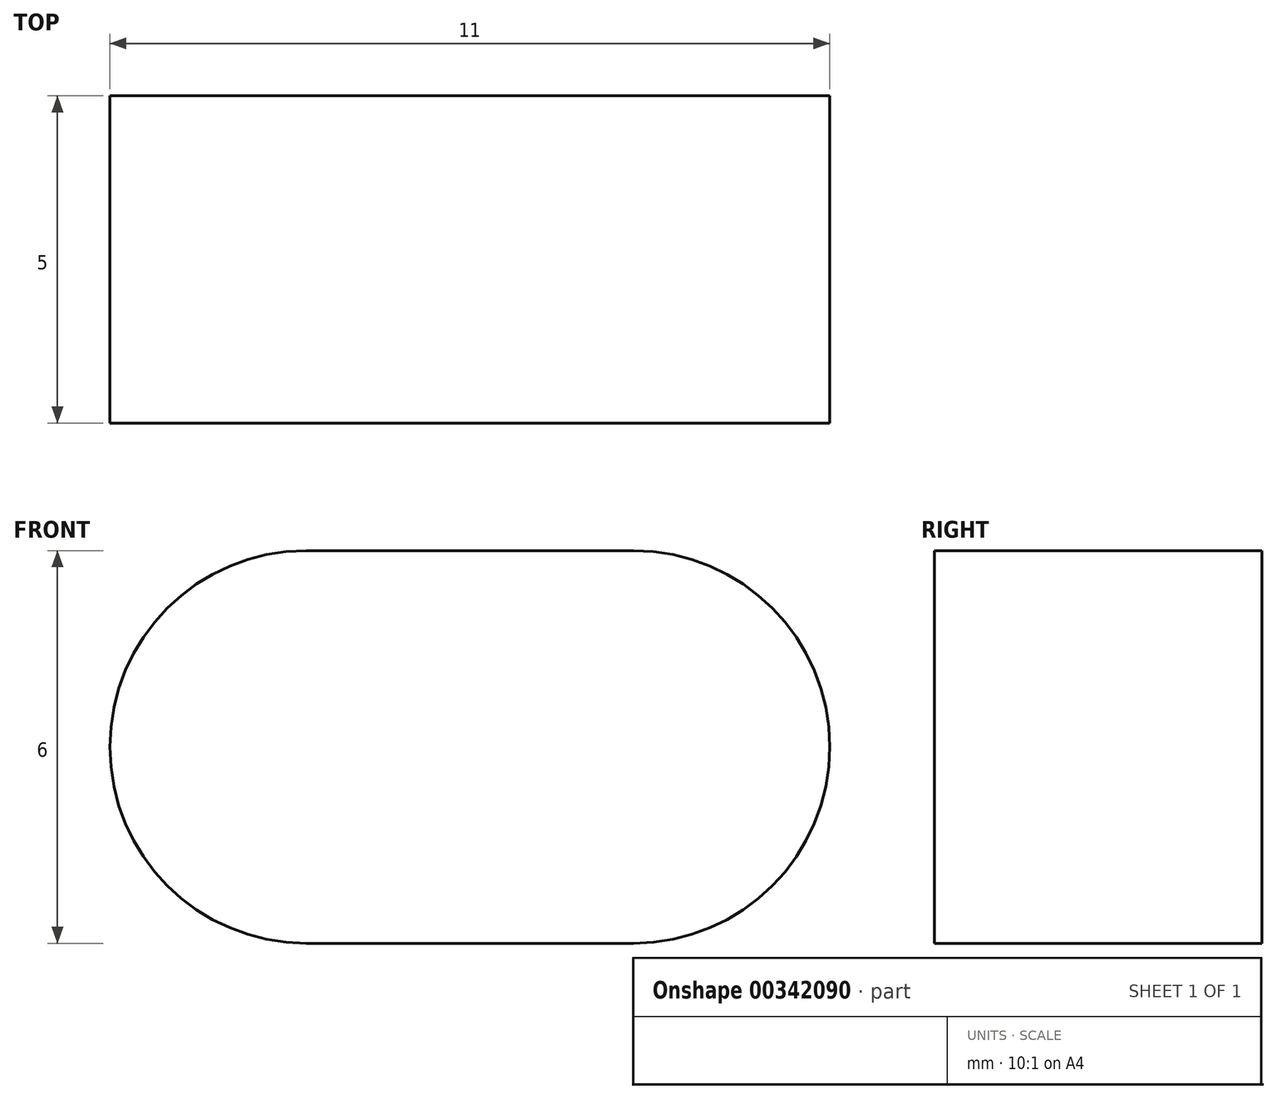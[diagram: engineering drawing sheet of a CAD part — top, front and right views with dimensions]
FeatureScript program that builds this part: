
annotation { "Feature Type Name" : "Feature", "Feature Type Description" : "" }
export const myFeature = defineFeature(function(context is Context, id is Id, definition is map)
    precondition{}
    {
        {
            var Q0;
            Q0=qCreatedBy(makeId("Front.planeOp"),FACE);
            var sketch = newSketch(context, id + "F0", { "sketchPlane" : qUnion([Q0])});
            skLineSegment(sketch, "E0.bottom", {"start": v(2.5, 3) * mm, "end": v(-2.5, 3) * mm});
            skLineSegment(sketch, "E0.top", {"start": v(2.5, -3) * mm, "end": v(-2.5, -3) * mm});
            skLineSegment(sketch, "E0.left", {"start": v(2.5, 3) * mm, "end": v(2.5, -3) * mm});
            skLineSegment(sketch, "E0.right", {"start": v(-2.5, 3) * mm, "end": v(-2.5, -3) * mm});
            skPoint(sketch, "E0.middle", {"position": v(0, 0) * mm});
            skArc(sketch, "E1", {"start": v(2.5, -3) * mm, "mid": v(5.5, 0) * mm, "end": v(2.5, 3) * mm});
            skArc(sketch, "E2", {"start": v(-2.5, 3) * mm, "mid": v(-5.5, 0) * mm, "end": v(-2.5, -3) * mm});
            skSolve(sketch);
        }
        {
            var Q0;
            Q0=qSketchRegion(id+"F0",true);
            extrude(context, id + "F1", {"entities" : qUnion([Q0]), "depth" : 5 * mm});
        }
    });
